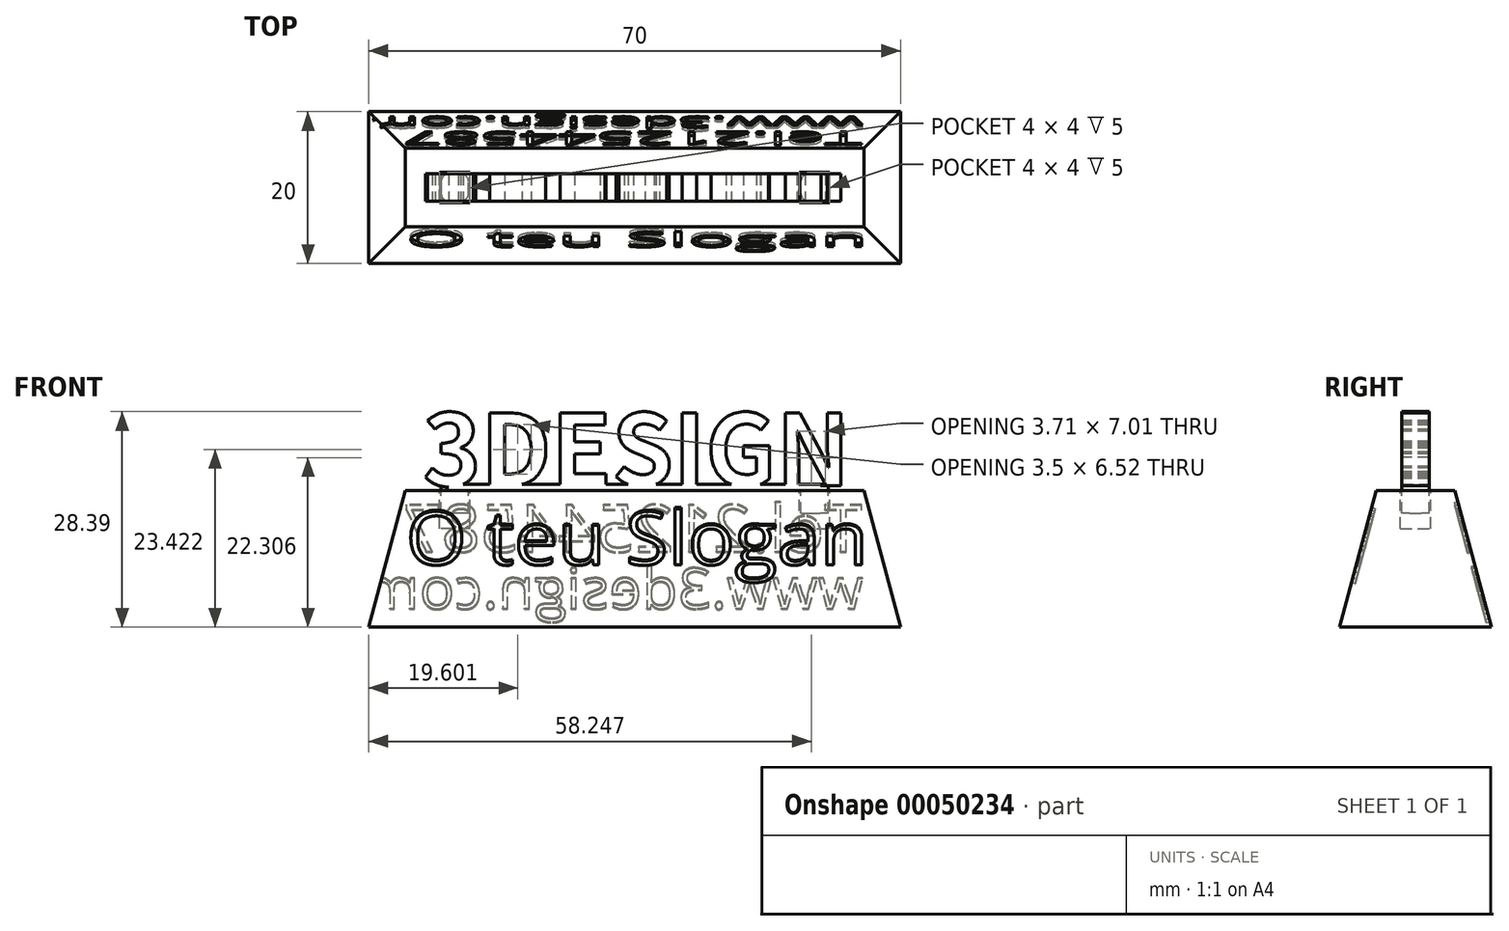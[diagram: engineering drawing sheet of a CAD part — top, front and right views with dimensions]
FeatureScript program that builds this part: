
annotation { "Feature Type Name" : "Feature", "Feature Type Description" : "" }
export const myFeature = defineFeature(function(context is Context, id is Id, definition is map)
    precondition{}
    {
        {
            var Q0;
            Q0=qCreatedBy(makeId("Top.planeOp"),FACE);
            var sketch = newSketch(context, id + "F0", { "sketchPlane" : qUnion([Q0])});
            skLineSegment(sketch, "E0.rect.bottom", {"start": v(35, 10) * mm, "end": v(-35, 10) * mm});
            skLineSegment(sketch, "E0.rect.top", {"start": v(35, -10) * mm, "end": v(-35, -10) * mm});
            skLineSegment(sketch, "E0.rect.left", {"start": v(35, 10) * mm, "end": v(35, -10) * mm});
            skLineSegment(sketch, "E0.rect.right", {"start": v(-35, 10) * mm, "end": v(-35, -10) * mm});
            skPoint(sketch, "E0.rect.middle", {"position": v(0, 0) * mm});
            skSolve(sketch);
        }
        {
            var Q0;
            Q0 = qSketchRegion(id + "F0", true);
            extrude(context, id + "F1", {"entities" : qUnion([Q0]), "depth" : 18 * mm, "hasDraft" : true, "draftAngle" : 15 * degree, "draftPullDirection" : true});
        }
        {
            var Q0;
            Q0=makeQuery(id+"F1.opExtrude","SWEPT_FACE",FACE,{"disambiguationData":[OSD([sQuery(id+"F0.wireOp",EDGE,"E0.rect.top")])]});
            var sketch = newSketch(context, id + "F2", { "sketchPlane" : qUnion([Q0])});
            skText(sketch, "E1", { "text": "O teu Slogan", "fontName": "OpenSans-Regular.ttf"});
            const initialGuessF2  = {"E1": [-0.0301, 0.00594, 1, 0, 0.00736]};
            skSetInitialGuess(sketch, initialGuessF2);
            skSolve(sketch);
        }
        {
            var Q0;
            Q0 = qSketchRegion(id + "F2", true);
            extrude(context, id + "F3", {"entities" : qUnion([Q0]), "operationType" : NewBodyOperationType.REMOVE, "oppositeDirection" : true, "depth" : 0.5 * mm});
        }
        {
            var Q0;
            Q0=makeQuery(id+"F1.opExtrude","SWEPT_FACE",FACE,{"disambiguationData":[OSD([sQuery(id+"F0.wireOp",EDGE,"E0.rect.bottom")])]});
            var sketch = newSketch(context, id + "F4", { "sketchPlane" : qUnion([Q0])});
            skText(sketch, "E2", { "text": "Tel.212544587\n", "fontName": "OpenSans-Regular.ttf"});
            skText(sketch, "E3", { "text": "www.3design.com", "fontName": "OpenSans-Regular.ttf"});
            const initialGuessF4  = {"E2": [-0.02992, 0.00776, 1, 0, 0.00642], "E3": [-0.03011, 0, 1, 0, 0.00555]};
            skSetInitialGuess(sketch, initialGuessF4);
            skSolve(sketch);
        }
        {
            var Q0;
            Q0 = qSketchRegion(id + "F4", true);
            extrude(context, id + "F5", {"entities" : qUnion([Q0]), "operationType" : NewBodyOperationType.REMOVE, "oppositeDirection" : true, "depth" : 0.5 * mm});
        }
        {
            var Q0;
            Q0=makeQuery(id+"F1.opExtrude","CAP_FACE",FACE,{"disambiguationData":[OSD([sQuery(id+"F0.wireOp",EDGE,"E0.rect.bottom"),sQuery(id+"F0.wireOp",EDGE,"E0.rect.top"),sQuery(id+"F0.wireOp",EDGE,"E0.rect.left"),sQuery(id+"F0.wireOp",EDGE,"E0.rect.right")])],"isStart":false});
            var sketch = newSketch(context, id + "F6", { "sketchPlane" : qUnion([Q0])});
            skLineSegment(sketch, "E4", {"start": v(0, 17.72) * mm, "end": v(0, -18) * mm, "construction": true});
            skLineSegment(sketch, "E5", {"start": v(40.48, 0) * mm, "end": v(-40.14, 0) * mm, "construction": true});
            skLineSegment(sketch, "E6.rect.bottom", {"start": v(21.69, -2) * mm, "end": v(25.69, -2) * mm});
            skLineSegment(sketch, "E6.rect.top", {"start": v(21.69, 2) * mm, "end": v(25.69, 2) * mm});
            skLineSegment(sketch, "E6.rect.left", {"start": v(21.69, -2) * mm, "end": v(21.69, 2) * mm});
            skLineSegment(sketch, "E6.rect.right", {"start": v(25.69, -2) * mm, "end": v(25.69, 2) * mm});
            skPoint(sketch, "E6.rect.middle", {"position": v(23.69, 0) * mm});
            skPoint(sketch, "E7.MirrorP", {"position": v(-23.69, 0) * mm});
            skLineSegment(sketch, "E8.MirrorCS", {"start": v(-21.69, -2) * mm, "end": v(-21.69, 2) * mm});
            skLineSegment(sketch, "E9.MirrorCS", {"start": v(-21.69, -2) * mm, "end": v(-25.69, -2) * mm});
            skLineSegment(sketch, "E10.MirrorCS", {"start": v(-21.69, 2) * mm, "end": v(-25.69, 2) * mm});
            skLineSegment(sketch, "E11.MirrorCS", {"start": v(-25.69, -2) * mm, "end": v(-25.69, 2) * mm});
            skSolve(sketch);
        }
        {
            var Q0;
            Q0 = qSketchRegion(id + "F6", true);
            extrude(context, id + "F7", {"entities" : qUnion([Q0]), "operationType" : NewBodyOperationType.REMOVE, "oppositeDirection" : true, "depth" : 5 * mm});
        }
        {
            var Q0;
            Q0=makeQuery(id+"F1.opExtrude","CAP_FACE",FACE,{"disambiguationData":[OSD([sQuery(id+"F0.wireOp",EDGE,"E0.rect.bottom"),sQuery(id+"F0.wireOp",EDGE,"E0.rect.top"),sQuery(id+"F0.wireOp",EDGE,"E0.rect.left"),sQuery(id+"F0.wireOp",EDGE,"E0.rect.right")])],"isStart":false});
            var sketch = newSketch(context, id + "F8", { "sketchPlane" : qUnion([Q0])});
            skLineSegment(sketch, "E12.0", {"start": v(21.89, 1.8) * mm, "end": v(25.49, 1.8) * mm});
            skLineSegment(sketch, "E12.1", {"start": v(21.89, -1.8) * mm, "end": v(21.89, 1.8) * mm});
            skLineSegment(sketch, "E12.2", {"start": v(21.89, -1.8) * mm, "end": v(25.49, -1.8) * mm});
            skLineSegment(sketch, "E12.3", {"start": v(25.49, -1.8) * mm, "end": v(25.49, 1.8) * mm});
            skLineSegment(sketch, "E13.0", {"start": v(-21.89, 1.8) * mm, "end": v(-25.49, 1.8) * mm});
            skLineSegment(sketch, "E13.1", {"start": v(-21.89, -1.8) * mm, "end": v(-21.89, 1.8) * mm});
            skLineSegment(sketch, "E13.2", {"start": v(-21.89, -1.8) * mm, "end": v(-25.49, -1.8) * mm});
            skLineSegment(sketch, "E13.3", {"start": v(-25.49, -1.8) * mm, "end": v(-25.49, 1.8) * mm});
            skPoint(sketch, "E14.0.end.orphan", {"position": v(-21.69, 2) * mm});
            skPoint(sketch, "E15.0.end.orphan", {"position": v(-25.69, 2) * mm});
            skPoint(sketch, "E16.0.end.orphan", {"position": v(-25.69, -2) * mm});
            skPoint(sketch, "E16.0.start.orphan", {"position": v(-21.69, -2) * mm});
            skPoint(sketch, "E17.0.end.orphan", {"position": v(21.69, 2) * mm});
            skPoint(sketch, "E18.0.end.orphan", {"position": v(25.69, 2) * mm});
            skPoint(sketch, "E19.0.end.orphan", {"position": v(25.69, -2) * mm});
            skPoint(sketch, "E19.0.start.orphan", {"position": v(21.69, -2) * mm});
            skSolve(sketch);
        }
        {
            var Q0;
            Q0 = qSketchRegion(id + "F8", true);
            extrude(context, id + "F9", {"entities" : qUnion([Q0]), "oppositeDirection" : true, "depth" : 3 * mm});
        }
        {
            var Q0;
            Q0=makeQuery(id+"F9.opExtrude","CAP_FACE",FACE,{"disambiguationData":[OSD([sQuery(id+"F8.wireOp",EDGE,"E13.0"),sQuery(id+"F8.wireOp",EDGE,"E13.1"),sQuery(id+"F8.wireOp",EDGE,"E13.2"),sQuery(id+"F8.wireOp",EDGE,"E13.3")])],"isStart":true});
            var sketch = newSketch(context, id + "F10", { "sketchPlane" : qUnion([Q0])});
            skPoint(sketch, "E20.0", {"position": v(25.49, -1.8) * mm});
            skLineSegment(sketch, "E21.bottom", {"start": v(-25.49, 1.8) * mm, "end": v(25.49, 1.8) * mm});
            skLineSegment(sketch, "E21.top", {"start": v(-25.49, -1.8) * mm, "end": v(25.49, -1.8) * mm});
            skLineSegment(sketch, "E21.left", {"start": v(-25.49, 1.8) * mm, "end": v(-25.49, -1.8) * mm});
            skLineSegment(sketch, "E21.right", {"start": v(25.49, 1.8) * mm, "end": v(25.49, -1.8) * mm});
            skSolve(sketch);
        }
        {
            var Q0;
            Q0 = qSketchRegion(id + "F10", true);
            extrude(context, id + "F11", {"entities" : qUnion([Q0]), "operationType" : NewBodyOperationType.ADD, "depth" : 0.8 * mm});
        }
        {
            var Q0;
            Q0=makeQuery(id+"F11.boolean.opBoolean","MERGE",FACE,{"derivedFrom":[makeQuery(id+"F9.opExtrude","SWEPT_FACE",FACE,{"disambiguationData":[OSD([sQuery(id+"F8.wireOp",EDGE,"E12.2")])]}),makeQuery(id+"F9.opExtrude","SWEPT_FACE",FACE,{"disambiguationData":[OSD([sQuery(id+"F8.wireOp",EDGE,"E13.2")])]}),makeQuery(id+"F11.opExtrude","SWEPT_FACE",FACE,{"disambiguationData":[OSD([sQuery(id+"F10.wireOp",EDGE,"E21.top")])]})]});
            var sketch = newSketch(context, id + "F12", { "sketchPlane" : qUnion([Q0])});
            skText(sketch, "E22", { "text": "3DESIGN", "fontName": "NotoSansCJKsc-Bold.otf"});
            const initialGuessF12  = {"E22": [-0.02788, 0.01862, 1, 0, 0.00933]};
            skSetInitialGuess(sketch, initialGuessF12);
            skSolve(sketch);
        }
        {
            var Q0;
            Q0 = qSketchRegion(id + "F12", true);
            var Q1;
            Q1=makeQuery(id+"F11.boolean.opBoolean","MERGE",FACE,{"derivedFrom":[makeQuery(id+"F9.opExtrude","SWEPT_FACE",FACE,{"disambiguationData":[OSD([sQuery(id+"F8.wireOp",EDGE,"E12.0")])]}),makeQuery(id+"F9.opExtrude","SWEPT_FACE",FACE,{"disambiguationData":[OSD([sQuery(id+"F8.wireOp",EDGE,"E13.0")])]}),makeQuery(id+"F11.opExtrude","SWEPT_FACE",FACE,{"disambiguationData":[OSD([sQuery(id+"F10.wireOp",EDGE,"E21.bottom")])]})]});
            extrude(context, id + "F13", {"entities" : qUnion([Q0]), "operationType" : NewBodyOperationType.ADD, "endBound" : BoundingType.UP_TO_SURFACE, "oppositeDirection" : true, "endBoundEntityFace" : qUnion([Q1]), "depth" : 25 * mm});
        }
        {
            var Q0;
            Q0=makeQuery(id+"F11.boolean.opBoolean","MERGE",EDGE,{"derivedFrom":[makeQuery(id+"F9.opExtrude","SWEPT_EDGE",EDGE,{"disambiguationData":[OSD([sQuery(id+"F8.wireOp",EDGE,"E12.0"),sQuery(id+"F8.wireOp",EDGE,"E12.3")])]}),makeQuery(id+"F11.opExtrude","SWEPT_EDGE",EDGE,{"disambiguationData":[OSD([sQuery(id+"F10.wireOp",EDGE,"E21.bottom"),sQuery(id+"F10.wireOp",EDGE,"E21.right")])]})]});
            var Q1;
            Q1=makeQuery(id+"F11.boolean.opBoolean","MERGE",EDGE,{"derivedFrom":[makeQuery(id+"F9.opExtrude","SWEPT_EDGE",EDGE,{"disambiguationData":[OSD([sQuery(id+"F8.wireOp",EDGE,"E12.2"),sQuery(id+"F8.wireOp",EDGE,"E12.3")])]}),makeQuery(id+"F11.opExtrude","SWEPT_EDGE",EDGE,{"disambiguationData":[OSD([sQuery(id+"F10.wireOp",EDGE,"E21.top"),sQuery(id+"F10.wireOp",EDGE,"E21.right")])]})]});
            var Q2;
            Q2=makeQuery(id+"F9.opExtrude","SWEPT_EDGE",EDGE,{"disambiguationData":[OSD([sQuery(id+"F8.wireOp",EDGE,"E12.0"),sQuery(id+"F8.wireOp",EDGE,"E12.1")])]});
            var Q3;
            Q3=makeQuery(id+"F9.opExtrude","SWEPT_EDGE",EDGE,{"disambiguationData":[OSD([sQuery(id+"F8.wireOp",EDGE,"E13.0"),sQuery(id+"F8.wireOp",EDGE,"E13.1")])]});
            var Q4;
            Q4=makeQuery(id+"F9.opExtrude","SWEPT_EDGE",EDGE,{"disambiguationData":[OSD([sQuery(id+"F8.wireOp",EDGE,"E13.1"),sQuery(id+"F8.wireOp",EDGE,"E13.2")])]});
            var Q5;
            Q5=makeQuery(id+"F9.opExtrude","SWEPT_EDGE",EDGE,{"disambiguationData":[OSD([sQuery(id+"F8.wireOp",EDGE,"E12.1"),sQuery(id+"F8.wireOp",EDGE,"E12.2")])]});
            var Q6;
            Q6=makeQuery(id+"F11.boolean.opBoolean","MERGE",EDGE,{"derivedFrom":[makeQuery(id+"F9.opExtrude","SWEPT_EDGE",EDGE,{"disambiguationData":[OSD([sQuery(id+"F8.wireOp",EDGE,"E13.2"),sQuery(id+"F8.wireOp",EDGE,"E13.3")])]}),makeQuery(id+"F11.opExtrude","SWEPT_EDGE",EDGE,{"disambiguationData":[OSD([sQuery(id+"F10.wireOp",EDGE,"E21.top"),sQuery(id+"F10.wireOp",EDGE,"E21.left")])]})]});
            var Q7;
            Q7=makeQuery(id+"F11.boolean.opBoolean","MERGE",EDGE,{"derivedFrom":[makeQuery(id+"F9.opExtrude","SWEPT_EDGE",EDGE,{"disambiguationData":[OSD([sQuery(id+"F8.wireOp",EDGE,"E13.0"),sQuery(id+"F8.wireOp",EDGE,"E13.3")])]}),makeQuery(id+"F11.opExtrude","SWEPT_EDGE",EDGE,{"disambiguationData":[OSD([sQuery(id+"F10.wireOp",EDGE,"E21.bottom"),sQuery(id+"F10.wireOp",EDGE,"E21.left")])]})]});
            fillet(context, id + "F14", {"entities" : qUnion([Q0, Q1, Q2, Q3, Q4, Q5, Q6, Q7]), "radius" : 1 * mm, "tangentPropagation" : true, "allowEdgeOverflow" : false});
        }
    });
